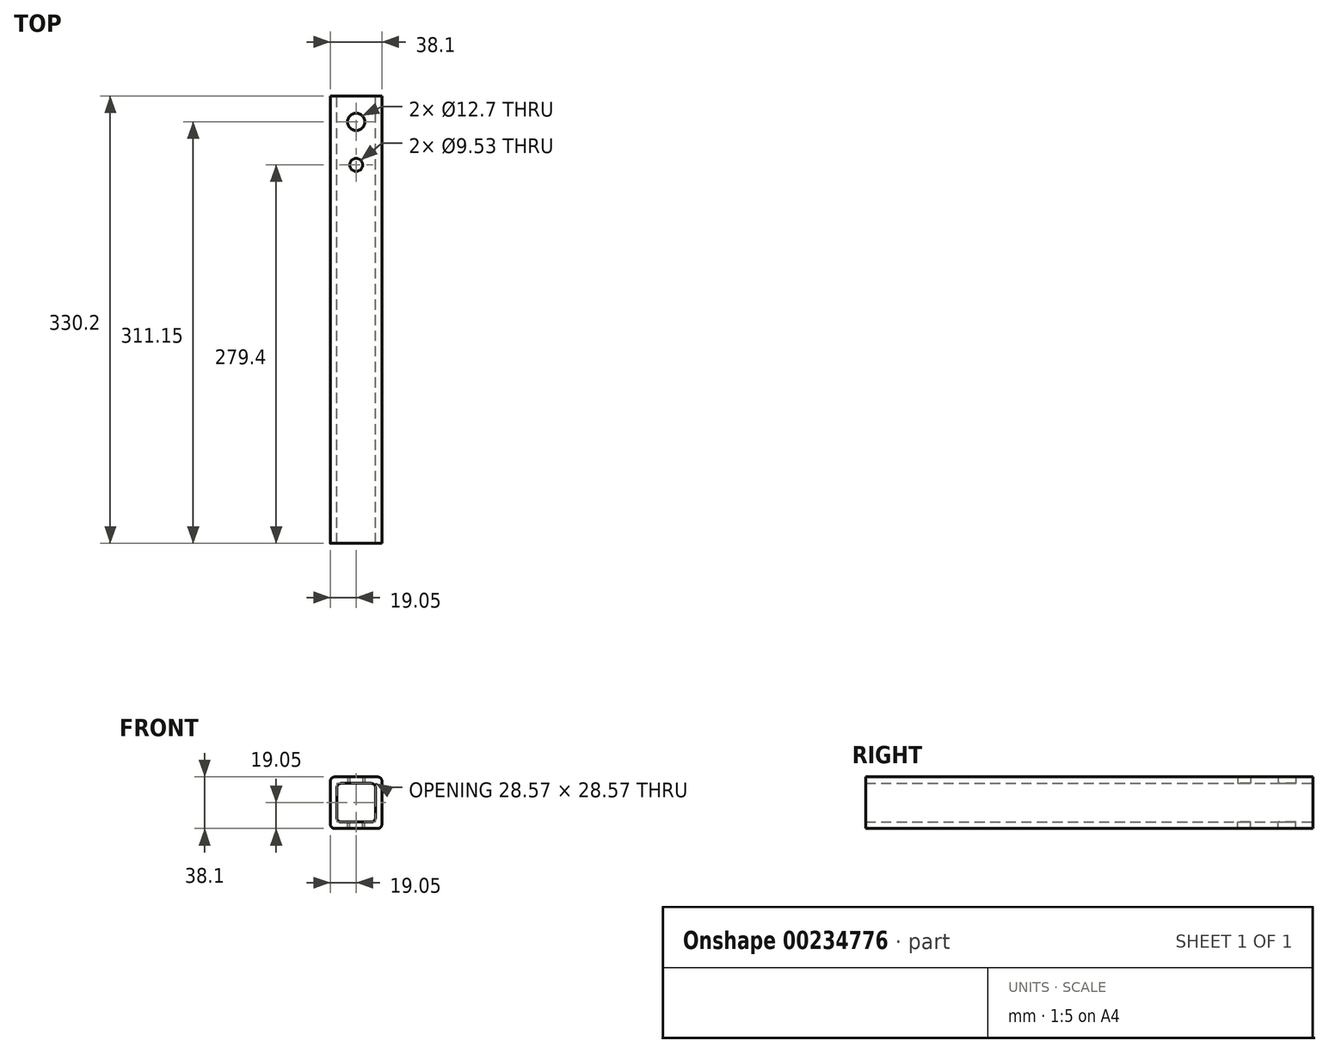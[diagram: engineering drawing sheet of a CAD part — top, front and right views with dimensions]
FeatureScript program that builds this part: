
annotation { "Feature Type Name" : "Feature", "Feature Type Description" : "" }
export const myFeature = defineFeature(function(context is Context, id is Id, definition is map)
    precondition{}
    {
        {
            var Q0;
            Q0=qCreatedBy(makeId("Front.planeOp"),FACE);
            var sketch = newSketch(context, id + "F0", { "sketchPlane" : qUnion([Q0])});
            skLineSegment(sketch, "E0.bottom", {"start": v(15.88, -19.05) * mm, "end": v(-15.88, -19.05) * mm});
            skLineSegment(sketch, "E0.top", {"start": v(15.88, 19.05) * mm, "end": v(-15.88, 19.05) * mm});
            skLineSegment(sketch, "E0.left", {"start": v(19.05, -15.88) * mm, "end": v(19.05, 15.88) * mm});
            skLineSegment(sketch, "E0.right", {"start": v(-19.05, -15.88) * mm, "end": v(-19.05, 15.87) * mm});
            skPoint(sketch, "E0.middle", {"position": v(0, 0) * mm});
            skLineSegment(sketch, "E1.bottom", {"start": v(11.11, -14.29) * mm, "end": v(-11.11, -14.29) * mm});
            skLineSegment(sketch, "E1.top", {"start": v(11.11, 14.29) * mm, "end": v(-11.11, 14.29) * mm});
            skLineSegment(sketch, "E1.left", {"start": v(14.29, -11.11) * mm, "end": v(14.29, 11.11) * mm});
            skLineSegment(sketch, "E1.right", {"start": v(-14.29, -11.11) * mm, "end": v(-14.29, 11.11) * mm});
            skPoint(sketch, "E2.visualSharp", {"position": v(-19.05, 19.05) * mm});
            skArc(sketch, "E2.filletArc", {"start": v(-15.88, 19.05) * mm, "mid": v(-18.12, 18.12) * mm, "end": v(-19.05, 15.87) * mm});
            skPoint(sketch, "E3.visualSharp", {"position": v(19.05, 19.05) * mm});
            skArc(sketch, "E3.filletArc", {"start": v(19.05, 15.88) * mm, "mid": v(18.12, 18.12) * mm, "end": v(15.88, 19.05) * mm});
            skPoint(sketch, "E4.visualSharp", {"position": v(14.29, 14.29) * mm});
            skArc(sketch, "E4.filletArc", {"start": v(14.29, 11.11) * mm, "mid": v(13.36, 13.36) * mm, "end": v(11.11, 14.29) * mm});
            skPoint(sketch, "E5.visualSharp", {"position": v(-14.29, 14.29) * mm});
            skArc(sketch, "E5.filletArc", {"start": v(-11.11, 14.29) * mm, "mid": v(-13.36, 13.36) * mm, "end": v(-14.29, 11.11) * mm});
            skPoint(sketch, "E6.visualSharp", {"position": v(-14.29, -14.29) * mm});
            skArc(sketch, "E6.filletArc", {"start": v(-14.29, -11.11) * mm, "mid": v(-13.36, -13.36) * mm, "end": v(-11.11, -14.29) * mm});
            skPoint(sketch, "E7.visualSharp", {"position": v(-19.05, -19.05) * mm});
            skArc(sketch, "E7.filletArc", {"start": v(-19.05, -15.88) * mm, "mid": v(-18.12, -18.12) * mm, "end": v(-15.88, -19.05) * mm});
            skPoint(sketch, "E8.visualSharp", {"position": v(14.29, -14.29) * mm});
            skArc(sketch, "E8.filletArc", {"start": v(11.11, -14.29) * mm, "mid": v(13.36, -13.36) * mm, "end": v(14.29, -11.11) * mm});
            skPoint(sketch, "E9.visualSharp", {"position": v(19.05, -19.05) * mm});
            skArc(sketch, "E9.filletArc", {"start": v(15.88, -19.05) * mm, "mid": v(18.12, -18.12) * mm, "end": v(19.05, -15.88) * mm});
            skSolve(sketch);
        }
        {
            var Q0;
            Q0=makeQuery(id+"F0.imprint","IMPRINT",FACE,{"disambiguationData":[TD([[makeQuery(id+"F0.imprint","IMPRINT",EDGE,{"derivedFrom":sQuery(id+"F0.wireOp",EDGE,"E0.bottom")}),-1.0]])]});
            extrude(context, id + "F3", {"entities" : qUnion([Q0]), "depth" : 330.2 * mm});
        }
        {
            var Q0;
            Q0=qCreatedBy(makeId("Top.planeOp"),FACE);
            var sketch = newSketch(context, id + "F1", { "sketchPlane" : qUnion([Q0])});
            skPoint(sketch, "E10", {"position": v(0, -19.05) * mm});
            skPoint(sketch, "E11", {"position": v(0, -50.8) * mm});
            skSolve(sketch);
        }
        {
            var Q0;
            Q0=sQuery(id+"F1.wireOp",VERTEX,"E10");
            var Q1;
            Q1=makeQuery(id+"F3.opExtrude","SWEPT_BODY",BODY,{"disambiguationData":[OSD([sQuery(id+"F0.wireOp",EDGE,"E0.bottom"),sQuery(id+"F0.wireOp",EDGE,"E0.top"),sQuery(id+"F0.wireOp",EDGE,"E0.left"),sQuery(id+"F0.wireOp",EDGE,"E0.right"),sQuery(id+"F0.wireOp",EDGE,"E1.bottom"),sQuery(id+"F0.wireOp",EDGE,"E1.top"),sQuery(id+"F0.wireOp",EDGE,"E1.left"),sQuery(id+"F0.wireOp",EDGE,"E1.right"),sQuery(id+"F0.wireOp",EDGE,"E2.filletArc"),sQuery(id+"F0.wireOp",EDGE,"E3.filletArc"),sQuery(id+"F0.wireOp",EDGE,"E4.filletArc"),sQuery(id+"F0.wireOp",EDGE,"E5.filletArc"),sQuery(id+"F0.wireOp",EDGE,"E6.filletArc"),sQuery(id+"F0.wireOp",EDGE,"E7.filletArc"),sQuery(id+"F0.wireOp",EDGE,"E8.filletArc"),sQuery(id+"F0.wireOp",EDGE,"E9.filletArc")])]});
            hole(context, id + "F4", {"style" : HoleStyle.SIMPLE, "endStyle" : HoleEndStyle.THROUGH, "holeDiameter" : 12.7 * mm, "locations" : qUnion([Q0]), "scope" : qUnion([Q1]), "isTappedThrough" : true});
        }
        {
            var Q0;
            Q0=sQuery(id+"F1.wireOp",VERTEX,"E10");
            var Q1;
            Q1=makeQuery(id+"F3.opExtrude","SWEPT_BODY",BODY,{"disambiguationData":[OSD([sQuery(id+"F0.wireOp",EDGE,"E0.bottom"),sQuery(id+"F0.wireOp",EDGE,"E0.top"),sQuery(id+"F0.wireOp",EDGE,"E0.left"),sQuery(id+"F0.wireOp",EDGE,"E0.right"),sQuery(id+"F0.wireOp",EDGE,"E1.bottom"),sQuery(id+"F0.wireOp",EDGE,"E1.top"),sQuery(id+"F0.wireOp",EDGE,"E1.left"),sQuery(id+"F0.wireOp",EDGE,"E1.right"),sQuery(id+"F0.wireOp",EDGE,"E2.filletArc"),sQuery(id+"F0.wireOp",EDGE,"E3.filletArc"),sQuery(id+"F0.wireOp",EDGE,"E4.filletArc"),sQuery(id+"F0.wireOp",EDGE,"E5.filletArc"),sQuery(id+"F0.wireOp",EDGE,"E6.filletArc"),sQuery(id+"F0.wireOp",EDGE,"E7.filletArc"),sQuery(id+"F0.wireOp",EDGE,"E8.filletArc"),sQuery(id+"F0.wireOp",EDGE,"E9.filletArc")])]});
            hole(context, id + "F5", {"style" : HoleStyle.SIMPLE, "endStyle" : HoleEndStyle.THROUGH, "oppositeDirection" : true, "holeDiameter" : 12.7 * mm, "locations" : qUnion([Q0]), "scope" : qUnion([Q1]), "isTappedThrough" : true});
        }
        {
            var Q0;
            Q0=sQuery(id+"F1.wireOp",VERTEX,"E11");
            var Q1;
            Q1=makeQuery(id+"F3.opExtrude","SWEPT_BODY",BODY,{"disambiguationData":[OSD([sQuery(id+"F0.wireOp",EDGE,"E0.bottom"),sQuery(id+"F0.wireOp",EDGE,"E0.top"),sQuery(id+"F0.wireOp",EDGE,"E0.left"),sQuery(id+"F0.wireOp",EDGE,"E0.right"),sQuery(id+"F0.wireOp",EDGE,"E1.bottom"),sQuery(id+"F0.wireOp",EDGE,"E1.top"),sQuery(id+"F0.wireOp",EDGE,"E1.left"),sQuery(id+"F0.wireOp",EDGE,"E1.right"),sQuery(id+"F0.wireOp",EDGE,"E2.filletArc"),sQuery(id+"F0.wireOp",EDGE,"E3.filletArc"),sQuery(id+"F0.wireOp",EDGE,"E4.filletArc"),sQuery(id+"F0.wireOp",EDGE,"E5.filletArc"),sQuery(id+"F0.wireOp",EDGE,"E6.filletArc"),sQuery(id+"F0.wireOp",EDGE,"E7.filletArc"),sQuery(id+"F0.wireOp",EDGE,"E8.filletArc"),sQuery(id+"F0.wireOp",EDGE,"E9.filletArc")])]});
            hole(context, id + "F6", {"style" : HoleStyle.SIMPLE, "endStyle" : HoleEndStyle.THROUGH, "holeDiameter" : 9.52 * mm, "locations" : qUnion([Q0]), "scope" : qUnion([Q1]), "isTappedThrough" : true});
        }
        {
            var Q0;
            Q0=sQuery(id+"F1.wireOp",VERTEX,"E11");
            var Q1;
            Q1=makeQuery(id+"F3.opExtrude","SWEPT_BODY",BODY,{"disambiguationData":[OSD([sQuery(id+"F0.wireOp",EDGE,"E0.bottom"),sQuery(id+"F0.wireOp",EDGE,"E0.top"),sQuery(id+"F0.wireOp",EDGE,"E0.left"),sQuery(id+"F0.wireOp",EDGE,"E0.right"),sQuery(id+"F0.wireOp",EDGE,"E1.bottom"),sQuery(id+"F0.wireOp",EDGE,"E1.top"),sQuery(id+"F0.wireOp",EDGE,"E1.left"),sQuery(id+"F0.wireOp",EDGE,"E1.right"),sQuery(id+"F0.wireOp",EDGE,"E2.filletArc"),sQuery(id+"F0.wireOp",EDGE,"E3.filletArc"),sQuery(id+"F0.wireOp",EDGE,"E4.filletArc"),sQuery(id+"F0.wireOp",EDGE,"E5.filletArc"),sQuery(id+"F0.wireOp",EDGE,"E6.filletArc"),sQuery(id+"F0.wireOp",EDGE,"E7.filletArc"),sQuery(id+"F0.wireOp",EDGE,"E8.filletArc"),sQuery(id+"F0.wireOp",EDGE,"E9.filletArc")])]});
            hole(context, id + "F2", {"style" : HoleStyle.SIMPLE, "endStyle" : HoleEndStyle.THROUGH, "oppositeDirection" : true, "holeDiameter" : 9.52 * mm, "locations" : qUnion([Q0]), "scope" : qUnion([Q1]), "isTappedThrough" : true});
        }
    });
